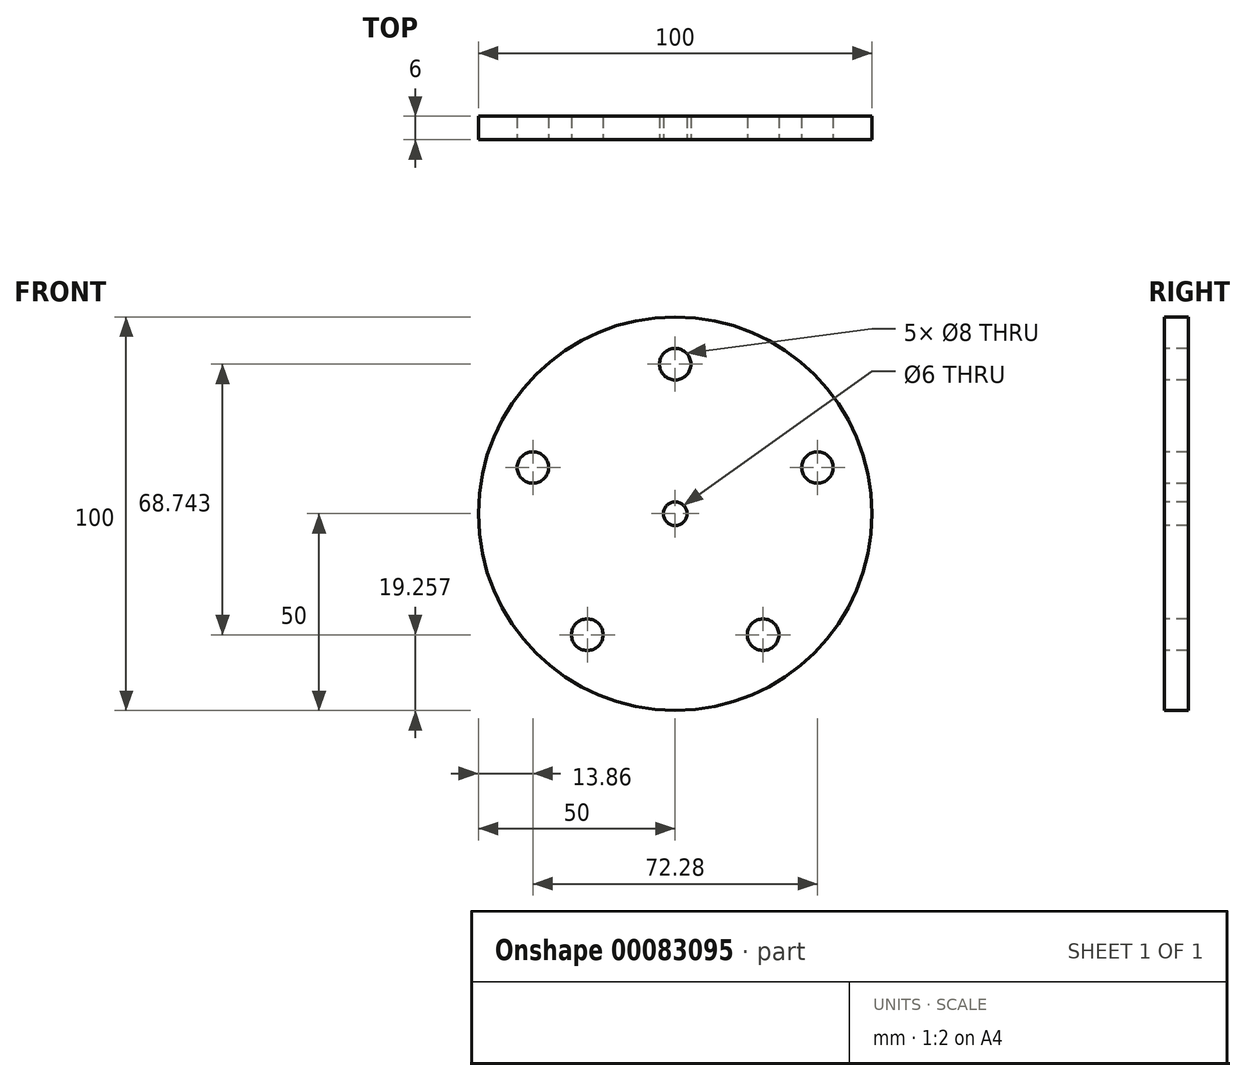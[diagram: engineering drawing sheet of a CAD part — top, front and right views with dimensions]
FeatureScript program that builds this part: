
annotation { "Feature Type Name" : "Feature", "Feature Type Description" : "" }
export const myFeature = defineFeature(function(context is Context, id is Id, definition is map)
    precondition{}
    {
        {
            var Q0;
            Q0=qCreatedBy(makeId("Front.planeOp"),FACE);
            var sketch = newSketch(context, id + "F0", { "sketchPlane" : qUnion([Q0])});
            skCircle(sketch, "E0", {"center": v(0, 0) * mm, "radius": 50 * mm});
            skSolve(sketch);
        }
        {
            var Q0;
            Q0 = qSketchRegion(id + "F0", true);
            extrude(context, id + "F1", {"entities" : qUnion([Q0]), "depth" : 6 * mm});
        }
        {
            var Q0;
            Q0=makeQuery(id+"F1.opExtrude","CAP_FACE",FACE,{"disambiguationData":[OSD([sQuery(id+"F0.wireOp",EDGE,"E0")])],"isStart":false});
            var sketch = newSketch(context, id + "F2", { "sketchPlane" : qUnion([Q0])});
            skCircle(sketch, "E1", {"center": v(0, 0) * mm, "radius": 3 * mm});
            skSolve(sketch);
        }
        {
            var Q0;
            Q0 = qSketchRegion(id + "F2", true);
            extrude(context, id + "F3", {"entities" : qUnion([Q0]), "operationType" : NewBodyOperationType.REMOVE, "endBound" : BoundingType.THROUGH_ALL, "oppositeDirection" : true, "depth" : 25 * mm});
        }
        {
            var Q0;
            Q0=makeQuery(id+"F1.opExtrude","CAP_FACE",FACE,{"disambiguationData":[OSD([sQuery(id+"F0.wireOp",EDGE,"E0")])],"isStart":false});
            var sketch = newSketch(context, id + "F4", { "sketchPlane" : qUnion([Q0])});
            skCircle(sketch, "E2", {"center": v(0, 38) * mm, "radius": 4 * mm});
            skCircle(sketch, "E3.1.0", {"center": v(-36.14, 11.74) * mm, "radius": 4 * mm});
            skCircle(sketch, "E3.2.0", {"center": v(-22.34, -30.74) * mm, "radius": 4 * mm});
            skPoint(sketch, "E3.center", {"position": v(0, 0) * mm});
            skCircle(sketch, "E4.1.3.0", {"center": v(22.34, -30.74) * mm, "radius": 4 * mm});
            skCircle(sketch, "E5.1.4.0", {"center": v(36.14, 11.74) * mm, "radius": 4 * mm});
            skSolve(sketch);
        }
        {
            var Q0;
            Q0=makeQuery(id+"F4.imprint","IMPRINT",FACE,{"disambiguationData":[TD([[makeQuery(id+"F4.imprint","IMPRINT",EDGE,{"derivedFrom":sQuery(id+"F4.wireOp",EDGE,"E2")}),1.0]])]});
            var Q1;
            Q1=makeQuery(id+"F4.imprint","IMPRINT",FACE,{"disambiguationData":[TD([[makeQuery(id+"F4.imprint","IMPRINT",EDGE,{"derivedFrom":sQuery(id+"F4.wireOp",EDGE,"E3.2.0")}),1.0]])]});
            var Q2;
            Q2=makeQuery(id+"F4.imprint","IMPRINT",FACE,{"disambiguationData":[TD([[makeQuery(id+"F4.imprint","IMPRINT",EDGE,{"derivedFrom":sQuery(id+"F4.wireOp",EDGE,"E3.1.0")}),1.0]])]});
            var Q3;
            Q3=makeQuery(id+"F4.imprint","IMPRINT",FACE,{"disambiguationData":[TD([[makeQuery(id+"F4.imprint","IMPRINT",EDGE,{"derivedFrom":sQuery(id+"F4.wireOp",EDGE,"E4.1.3.0")}),1.0]])]});
            var Q4;
            Q4=makeQuery(id+"F4.imprint","IMPRINT",FACE,{"disambiguationData":[TD([[makeQuery(id+"F4.imprint","IMPRINT",EDGE,{"derivedFrom":sQuery(id+"F4.wireOp",EDGE,"E5.1.4.0")}),1.0]])]});
            extrude(context, id + "F5", {"entities" : qUnion([Q0, Q1, Q2, Q3, Q4]), "operationType" : NewBodyOperationType.REMOVE, "endBound" : BoundingType.THROUGH_ALL, "oppositeDirection" : true, "depth" : 25 * mm});
        }
    });
